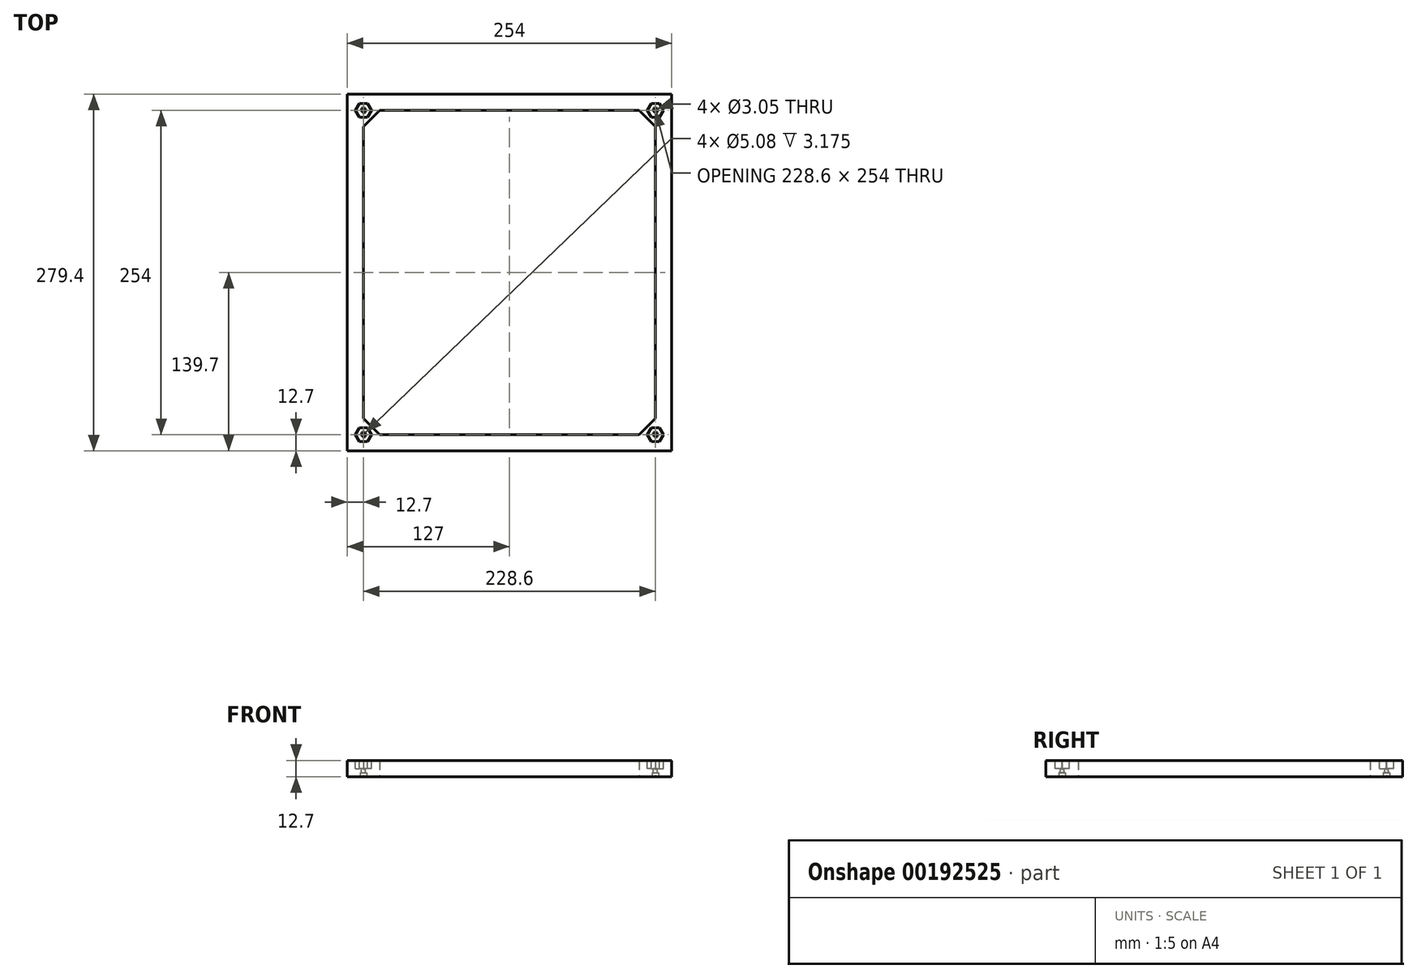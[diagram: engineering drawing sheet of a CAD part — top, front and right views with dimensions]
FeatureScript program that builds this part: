
annotation { "Feature Type Name" : "Feature", "Feature Type Description" : "" }
export const myFeature = defineFeature(function(context is Context, id is Id, definition is map)
    precondition{}
    {
        {
            var Q0;
            Q0=qCreatedBy(makeId("Top.planeOp"),FACE);
            var sketch = newSketch(context, id + "F0", { "sketchPlane" : qUnion([Q0])});
            skLineSegment(sketch, "E0.bottom", {"start": v(101.6, 127) * mm, "end": v(-101.6, 127) * mm});
            skLineSegment(sketch, "E0.top", {"start": v(101.6, -127) * mm, "end": v(-101.6, -127) * mm});
            skLineSegment(sketch, "E0.left", {"start": v(114.3, 114.3) * mm, "end": v(114.3, -114.3) * mm});
            skLineSegment(sketch, "E0.right", {"start": v(-114.3, 114.3) * mm, "end": v(-114.3, -114.3) * mm});
            skPoint(sketch, "E0.middle", {"position": v(0, 0) * mm});
            skLineSegment(sketch, "E1.bottom", {"start": v(127, 139.7) * mm, "end": v(-127, 139.7) * mm});
            skLineSegment(sketch, "E1.top", {"start": v(127, -139.7) * mm, "end": v(-127, -139.7) * mm});
            skLineSegment(sketch, "E1.left", {"start": v(127, 139.7) * mm, "end": v(127, -139.7) * mm});
            skLineSegment(sketch, "E1.right", {"start": v(-127, 139.7) * mm, "end": v(-127, -139.7) * mm});
            skLineSegment(sketch, "E2.bottom", {"start": v(-127, -139.7) * mm, "end": v(-101.6, -139.7) * mm});
            skLineSegment(sketch, "E2.left", {"start": v(-127, -139.7) * mm, "end": v(-127, -114.3) * mm});
            skLineSegment(sketch, "E3.bottom", {"start": v(127, -139.7) * mm, "end": v(101.6, -139.7) * mm});
            skLineSegment(sketch, "E3.left", {"start": v(127, -139.7) * mm, "end": v(127, -114.3) * mm});
            skLineSegment(sketch, "E4.bottom", {"start": v(-127, 139.7) * mm, "end": v(-101.6, 139.7) * mm});
            skLineSegment(sketch, "E4.left", {"start": v(-127, 139.7) * mm, "end": v(-127, 114.3) * mm});
            skLineSegment(sketch, "E5.bottom", {"start": v(127, 139.7) * mm, "end": v(101.6, 139.7) * mm});
            skLineSegment(sketch, "E5.left", {"start": v(127, 139.7) * mm, "end": v(127, 114.3) * mm});
            skPoint(sketch, "E6.orphan", {"position": v(-114.3, -127) * mm});
            skPoint(sketch, "E7.orphan", {"position": v(114.3, -127) * mm});
            skPoint(sketch, "E8.orphan", {"position": v(114.3, 127) * mm});
            skPoint(sketch, "E9.orphan", {"position": v(-114.3, 127) * mm});
            skLineSegment(sketch, "E10", {"start": v(-114.3, 114.3) * mm, "end": v(-101.6, 127) * mm});
            skLineSegment(sketch, "E11", {"start": v(114.3, 114.3) * mm, "end": v(101.6, 127) * mm});
            skLineSegment(sketch, "E12", {"start": v(114.3, -114.3) * mm, "end": v(101.6, -127) * mm});
            skLineSegment(sketch, "E13", {"start": v(-101.6, -127) * mm, "end": v(-114.3, -114.3) * mm});
            skSolve(sketch);
        }
        {
            var Q0;
            Q0=makeQuery(id+"F0.imprint","IMPRINT",FACE,{"disambiguationData":[TD([[makeQuery(id+"F0.imprint","IMPRINT",EDGE,{"derivedFrom":sQuery(id+"F0.wireOp",EDGE,"E0.bottom")}),-1.0]])]});
            extrude(context, id + "F1", {"entities" : qUnion([Q0]), "depth" : 12.7 * mm});
        }
        {
            var Q0;
            Q0=makeQuery(id+"F1.opExtrude","CAP_FACE",FACE,{"disambiguationData":[OSD([sQuery(id+"F0.wireOp",EDGE,"E0.bottom"),sQuery(id+"F0.wireOp",EDGE,"E0.top"),sQuery(id+"F0.wireOp",EDGE,"E0.left"),sQuery(id+"F0.wireOp",EDGE,"E0.right"),sQuery(id+"F0.wireOp",EDGE,"E1.bottom"),sQuery(id+"F0.wireOp",EDGE,"E1.top"),sQuery(id+"F0.wireOp",EDGE,"E1.left"),sQuery(id+"F0.wireOp",EDGE,"E1.right"),sQuery(id+"F0.wireOp",EDGE,"E2.bottom"),sQuery(id+"F0.wireOp",EDGE,"E2.top"),sQuery(id+"F0.wireOp",EDGE,"E2.left"),sQuery(id+"F0.wireOp",EDGE,"E2.right"),sQuery(id+"F0.wireOp",EDGE,"E3.bottom"),sQuery(id+"F0.wireOp",EDGE,"E3.top"),sQuery(id+"F0.wireOp",EDGE,"E3.left"),sQuery(id+"F0.wireOp",EDGE,"E3.right"),sQuery(id+"F0.wireOp",EDGE,"E4.bottom"),sQuery(id+"F0.wireOp",EDGE,"E4.top"),sQuery(id+"F0.wireOp",EDGE,"E4.left"),sQuery(id+"F0.wireOp",EDGE,"E4.right"),sQuery(id+"F0.wireOp",EDGE,"E5.bottom"),sQuery(id+"F0.wireOp",EDGE,"E5.top"),sQuery(id+"F0.wireOp",EDGE,"E5.left"),sQuery(id+"F0.wireOp",EDGE,"E5.right")])],"isStart":false});
            var sketch = newSketch(context, id + "F2", { "sketchPlane" : qUnion([Q0])});
            skCircle(sketch, "E14.cCircle", {"center": v(114.3, -127) * mm, "radius": 6.35 * mm, "construction": true});
            skLineSegment(sketch, "E14.0", {"start": v(107.95, -127) * mm, "end": v(111.12, -132.5) * mm});
            skLineSegment(sketch, "E14.1", {"start": v(111.13, -121.5) * mm, "end": v(107.95, -127) * mm});
            skLineSegment(sketch, "E14.2", {"start": v(117.48, -121.5) * mm, "end": v(111.13, -121.5) * mm});
            skLineSegment(sketch, "E14.3", {"start": v(120.65, -127) * mm, "end": v(117.48, -121.5) * mm});
            skLineSegment(sketch, "E14.4", {"start": v(117.48, -132.5) * mm, "end": v(120.65, -127) * mm});
            skLineSegment(sketch, "E14.5", {"start": v(111.12, -132.5) * mm, "end": v(117.47, -132.5) * mm});
            skCircle(sketch, "E15.cCircle", {"center": v(-114.3, -127) * mm, "radius": 6.35 * mm, "construction": true});
            skPoint(sketch, "E15.cCircle.perimeterSnap0", {"position": v(114.3, -132.5) * mm});
            skLineSegment(sketch, "E15.0", {"start": v(-111.12, -132.5) * mm, "end": v(-117.47, -132.5) * mm});
            skPoint(sketch, "E15.0.startSnap0", {"position": v(114.3, -132.5) * mm});
            skLineSegment(sketch, "E15.1", {"start": v(-117.47, -132.5) * mm, "end": v(-120.65, -127) * mm});
            skLineSegment(sketch, "E15.2", {"start": v(-120.65, -127) * mm, "end": v(-117.47, -121.5) * mm});
            skLineSegment(sketch, "E15.3", {"start": v(-117.47, -121.5) * mm, "end": v(-111.13, -121.5) * mm});
            skLineSegment(sketch, "E15.4", {"start": v(-111.13, -121.5) * mm, "end": v(-107.95, -127) * mm});
            skLineSegment(sketch, "E15.5", {"start": v(-107.95, -127) * mm, "end": v(-111.12, -132.5) * mm});
            skCircle(sketch, "E16.cCircle", {"center": v(-114.3, 127) * mm, "radius": 6.35 * mm, "construction": true});
            skLineSegment(sketch, "E16.0", {"start": v(-111.12, 132.5) * mm, "end": v(-107.95, 127) * mm});
            skLineSegment(sketch, "E16.1", {"start": v(-107.95, 127) * mm, "end": v(-111.12, 121.5) * mm});
            skLineSegment(sketch, "E16.2", {"start": v(-111.12, 121.5) * mm, "end": v(-117.48, 121.5) * mm});
            skLineSegment(sketch, "E16.3", {"start": v(-117.48, 121.5) * mm, "end": v(-120.65, 127) * mm});
            skLineSegment(sketch, "E16.4", {"start": v(-120.65, 127) * mm, "end": v(-117.48, 132.5) * mm});
            skLineSegment(sketch, "E16.5", {"start": v(-117.47, 132.5) * mm, "end": v(-111.12, 132.5) * mm});
            skCircle(sketch, "E17.cCircle", {"center": v(114.3, 127) * mm, "radius": 6.35 * mm, "construction": true});
            skLineSegment(sketch, "E17.0", {"start": v(117.48, 132.5) * mm, "end": v(120.65, 127) * mm});
            skLineSegment(sketch, "E17.1", {"start": v(120.65, 127) * mm, "end": v(117.48, 121.5) * mm});
            skLineSegment(sketch, "E17.2", {"start": v(117.48, 121.5) * mm, "end": v(111.13, 121.5) * mm});
            skLineSegment(sketch, "E17.3", {"start": v(111.12, 121.5) * mm, "end": v(107.95, 127) * mm});
            skLineSegment(sketch, "E17.4", {"start": v(107.95, 127) * mm, "end": v(111.13, 132.5) * mm});
            skLineSegment(sketch, "E17.5", {"start": v(111.13, 132.5) * mm, "end": v(117.48, 132.5) * mm});
            skSolve(sketch);
        }
        {
            var Q0;
            Q0 = qSketchRegion(id + "F2", true);
            extrude(context, id + "F3", {"entities" : qUnion([Q0]), "operationType" : NewBodyOperationType.REMOVE, "oppositeDirection" : true, "depth" : 6.35 * mm});
        }
        {
            var Q0;
            Q0=makeQuery(id+"F3.boolean.opBoolean","COPY",FACE,{"derivedFrom":makeQuery(id+"F3.opExtrude","CAP_FACE",FACE,{"disambiguationData":[OSD([sQuery(id+"F2.wireOp",EDGE,"E16.0"),sQuery(id+"F2.wireOp",EDGE,"E16.1"),sQuery(id+"F2.wireOp",EDGE,"E16.2"),sQuery(id+"F2.wireOp",EDGE,"E16.3"),sQuery(id+"F2.wireOp",EDGE,"E16.4"),sQuery(id+"F2.wireOp",EDGE,"E16.5")])],"isStart":false})});
            var sketch = newSketch(context, id + "F4", { "sketchPlane" : qUnion([Q0])});
            skCircle(sketch, "E18", {"center": v(-114.3, 127) * mm, "radius": 1.52 * mm});
            skCircle(sketch, "E19", {"center": v(114.3, 127) * mm, "radius": 1.52 * mm});
            skCircle(sketch, "E20", {"center": v(114.3, -127) * mm, "radius": 1.52 * mm});
            skCircle(sketch, "E21", {"center": v(-114.3, -127) * mm, "radius": 1.52 * mm});
            skSolve(sketch);
        }
        {
            var Q0;
            Q0 = qSketchRegion(id + "F4", true);
            extrude(context, id + "F5", {"entities" : qUnion([Q0]), "operationType" : NewBodyOperationType.REMOVE, "endBound" : BoundingType.THROUGH_ALL, "oppositeDirection" : true, "depth" : 25.4 * mm});
        }
        {
            var Q0;
            Q0=makeQuery(id+"F1.opExtrude","CAP_FACE",FACE,{"disambiguationData":[OSD([sQuery(id+"F0.wireOp",EDGE,"E0.bottom"),sQuery(id+"F0.wireOp",EDGE,"E0.top"),sQuery(id+"F0.wireOp",EDGE,"E0.left"),sQuery(id+"F0.wireOp",EDGE,"E0.right"),sQuery(id+"F0.wireOp",EDGE,"E1.bottom"),sQuery(id+"F0.wireOp",EDGE,"E1.top"),sQuery(id+"F0.wireOp",EDGE,"E1.left"),sQuery(id+"F0.wireOp",EDGE,"E1.right"),sQuery(id+"F0.wireOp",EDGE,"E2.bottom"),sQuery(id+"F0.wireOp",EDGE,"E2.left"),sQuery(id+"F0.wireOp",EDGE,"E3.bottom"),sQuery(id+"F0.wireOp",EDGE,"E3.left"),sQuery(id+"F0.wireOp",EDGE,"E4.bottom"),sQuery(id+"F0.wireOp",EDGE,"E4.left"),sQuery(id+"F0.wireOp",EDGE,"E5.bottom"),sQuery(id+"F0.wireOp",EDGE,"E5.left"),sQuery(id+"F0.wireOp",EDGE,"E10"),sQuery(id+"F0.wireOp",EDGE,"E11"),sQuery(id+"F0.wireOp",EDGE,"E12"),sQuery(id+"F0.wireOp",EDGE,"E13")])],"isStart":true});
            var sketch = newSketch(context, id + "F6", { "sketchPlane" : qUnion([Q0])});
            skCircle(sketch, "E22", {"center": v(-114.3, 127) * mm, "radius": 2.54 * mm});
            skCircle(sketch, "E23", {"center": v(114.3, 127) * mm, "radius": 2.54 * mm});
            skCircle(sketch, "E24", {"center": v(-114.3, -127) * mm, "radius": 2.54 * mm});
            skCircle(sketch, "E25", {"center": v(114.3, -127) * mm, "radius": 2.54 * mm});
            skSolve(sketch);
        }
        {
            var Q0;
            Q0 = qSketchRegion(id + "F6", true);
            extrude(context, id + "F7", {"entities" : qUnion([Q0]), "operationType" : NewBodyOperationType.REMOVE, "oppositeDirection" : true, "depth" : 3.17 * mm});
        }
    });
